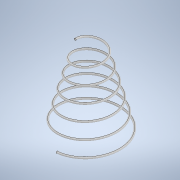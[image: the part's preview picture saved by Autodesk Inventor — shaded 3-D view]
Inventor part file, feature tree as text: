
AUTODESK INVENTOR PART (.ipt)
format: ipt  version: 2020 (Build 240168000, 168)  size: 259,072 bytes
history: native  units: mm
features: other x2, sketch x2, sweep x1
ambient origin geometry x8: Origin, YZ Plane, XZ Plane, XY Plane, X Axis, Y Axis, Z Axis, Center Point
bodies: Solid1 (feature_tree)
feature tree (5):
  sweep  "Sweep1"
  other  "Work Axis1"
  sketch  "3D Sketch1"
  other  "Helical Curve1"
  sketch  "Sketch2"  dims[d0=2.0mm d1=57.83mm d2=10.0mm d3=-2.617994mm d4=0.3mm d5=0.0mm d6=0.0mm]
